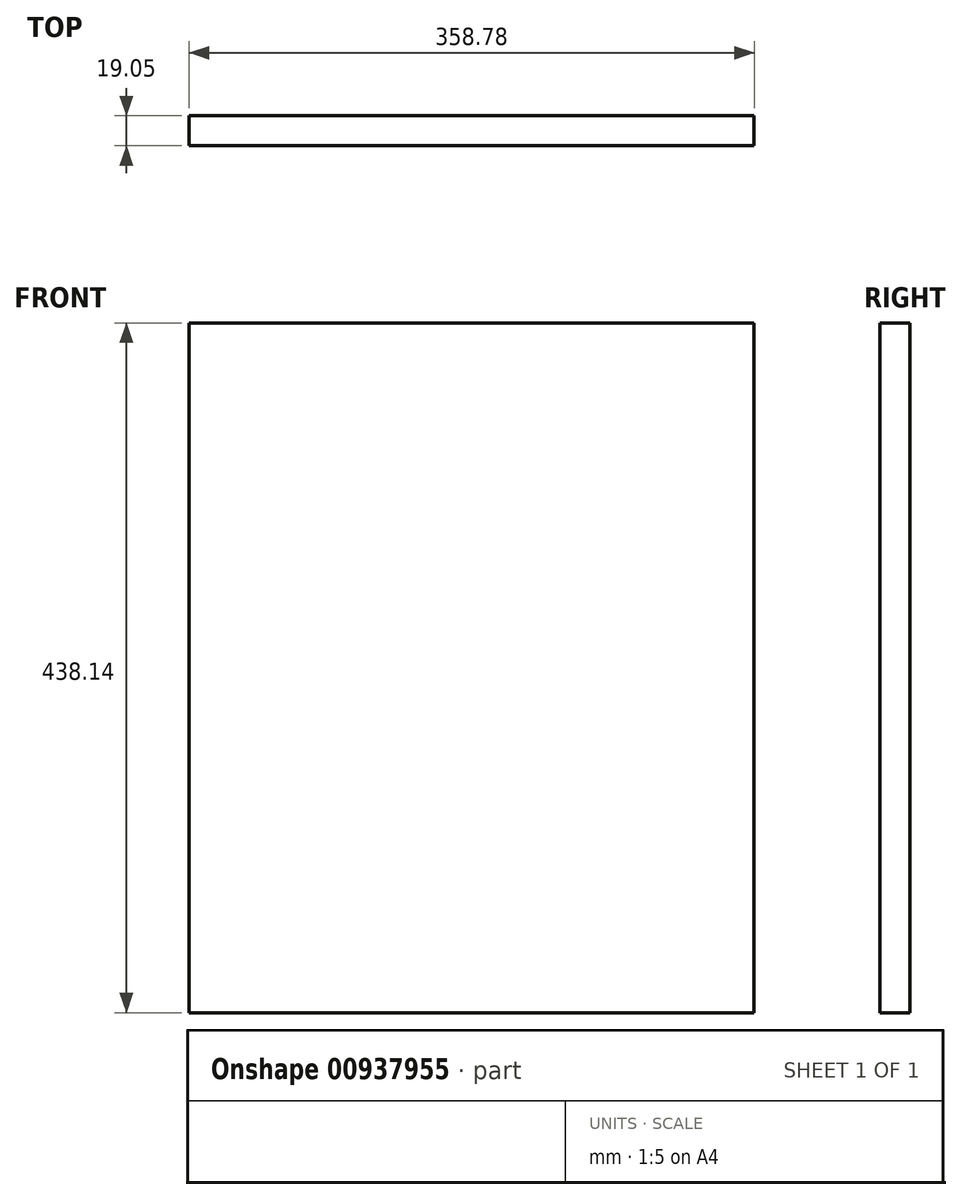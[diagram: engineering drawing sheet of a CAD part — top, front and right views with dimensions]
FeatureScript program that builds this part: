
annotation { "Feature Type Name" : "Feature", "Feature Type Description" : "" }
export const myFeature = defineFeature(function(context is Context, id is Id, definition is map)
    precondition{}
    {
        {
            var Q0;
            Q0=qCreatedBy(makeId("Front.planeOp"),FACE);
            var sketch = newSketch(context, id + "F0", { "sketchPlane" : qUnion([Q0])});
            skLineSegment(sketch, "E0.bottom", {"start": v(179.39, 219.08) * mm, "end": v(-179.39, 219.08) * mm});
            skLineSegment(sketch, "E0.top", {"start": v(179.39, -219.07) * mm, "end": v(-179.39, -219.07) * mm});
            skLineSegment(sketch, "E0.left", {"start": v(179.39, 219.08) * mm, "end": v(179.39, -219.07) * mm});
            skLineSegment(sketch, "E0.right", {"start": v(-179.39, 219.08) * mm, "end": v(-179.39, -219.07) * mm});
            skPoint(sketch, "E0.middle", {"position": v(0, 0) * mm});
            skSolve(sketch);
        }
        {
            var Q0;
            Q0=makeQuery(id+"F0.imprint","IMPRINT",FACE,{"disambiguationData":[TD([[makeQuery(id+"F0.imprint","IMPRINT",EDGE,{"derivedFrom":sQuery(id+"F0.wireOp",EDGE,"E0.bottom")}),1.0]])]});
            extrude(context, id + "F1", {"entities" : qUnion([Q0]), "depth" : 19.05 * mm, "offsetDistance" : 25.4 * mm});
        }
    });
